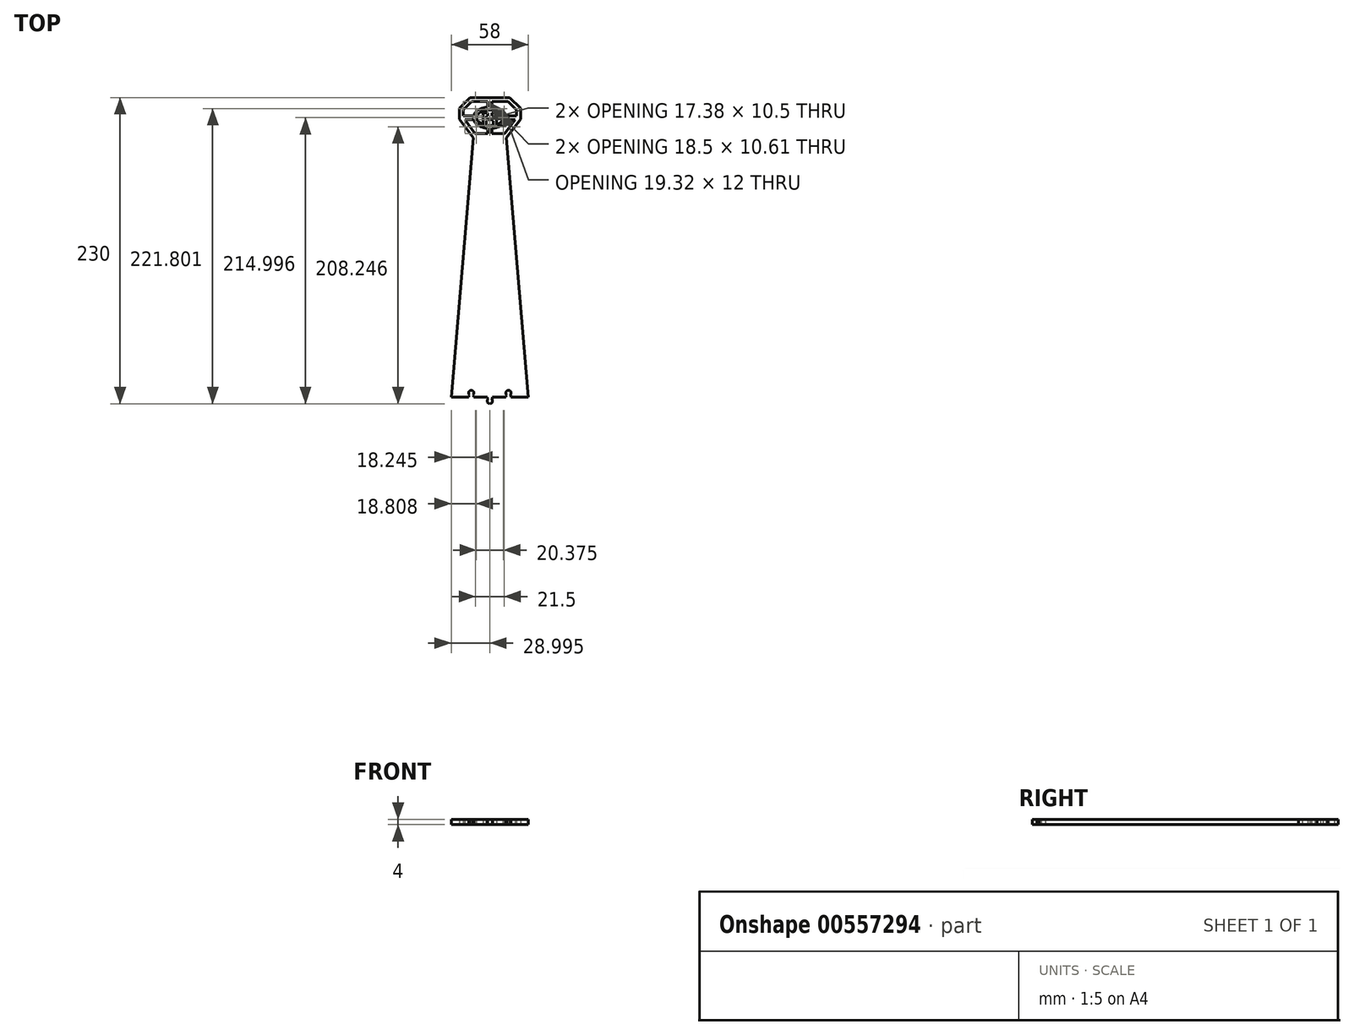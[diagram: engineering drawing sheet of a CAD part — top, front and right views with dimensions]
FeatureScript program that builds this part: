
annotation { "Feature Type Name" : "Feature", "Feature Type Description" : "" }
export const myFeature = defineFeature(function(context is Context, id is Id, definition is map)
    precondition{}
    {
        {
            var Q0;
            Q0=qCreatedBy(makeId("Top.planeOp"),FACE);
            var sketch = newSketch(context, id + "F0", { "sketchPlane" : qUnion([Q0])});
            skLineSegment(sketch, "E0.bottom", {"start": v(14.64, 150.88) * mm, "end": v(-15.36, 150.88) * mm});
            skLineSegment(sketch, "E0.top", {"start": v(12.14, 120.88) * mm, "end": v(-12.86, 120.88) * mm});
            skPoint(sketch, "E0.middle", {"position": v(-0.36, 135.88) * mm});
            skPoint(sketch, "E1", {"position": v(-0.36, 120.88) * mm});
            skPoint(sketch, "E2", {"position": v(-12.86, 120.88) * mm});
            skPoint(sketch, "E3", {"position": v(12.14, 120.88) * mm});
            skLineSegment(sketch, "E4", {"start": v(-15.36, 150.88) * mm, "end": v(-23.36, 142.88) * mm});
            skLineSegment(sketch, "E5", {"start": v(14.64, 150.88) * mm, "end": v(22.64, 142.88) * mm});
            skLineSegment(sketch, "E6", {"start": v(22.64, 142.88) * mm, "end": v(22.64, 134.88) * mm});
            skLineSegment(sketch, "E7", {"start": v(-23.36, 142.88) * mm, "end": v(-23.36, 134.88) * mm});
            skLineSegment(sketch, "E8", {"start": v(-23.36, 134.88) * mm, "end": v(-12.86, 120.88) * mm});
            skLineSegment(sketch, "E9", {"start": v(12.14, 120.88) * mm, "end": v(22.64, 134.88) * mm});
            skPoint(sketch, "E10.orphan", {"position": v(-15.36, 120.88) * mm});
            skEllipticalArc(sketch, "E11", {});
            skEllipticalArc(sketch, "E12", {});
            skLineSegment(sketch, "E13", {"start": v(13.28, 147.99) * mm, "end": v(1.14, 147.99) * mm});
            skLineSegment(sketch, "E14", {"start": v(10.64, 123.88) * mm, "end": v(1.14, 123.88) * mm});
            skLineSegment(sketch, "E15", {"start": v(19.64, 141.63) * mm, "end": v(19.64, 137.38) * mm});
            skLineSegment(sketch, "E16", {"start": v(-11.36, 123.88) * mm, "end": v(-19.24, 134.38) * mm});
            skLineSegment(sketch, "E17", {"start": v(-20.36, 141.63) * mm, "end": v(-20.36, 137.38) * mm});
            skLineSegment(sketch, "E18", {"start": v(-14.01, 147.99) * mm, "end": v(-20.36, 141.63) * mm});
            skLineSegment(sketch, "E19.trimOffspring", {"start": v(19.64, 141.63) * mm, "end": v(13.28, 147.99) * mm});
            skLineSegment(sketch, "E20.trimOffspring", {"start": v(10.64, 123.88) * mm, "end": v(18.51, 134.38) * mm});
            skPoint(sketch, "E21", {"position": v(-0.36, 147.99) * mm});
            skPoint(sketch, "E22", {"position": v(-0.36, 123.88) * mm});
            skPoint(sketch, "E23", {"position": v(-12.86, 135.88) * mm});
            skPoint(sketch, "E24", {"position": v(12.14, 135.88) * mm});
            skLineSegment(sketch, "E25", {"start": v(1.14, 147.99) * mm, "end": v(1.14, 143.82) * mm});
            skLineSegment(sketch, "E26.trimOffspring", {"start": v(1.14, 127.93) * mm, "end": v(1.14, 123.88) * mm});
            skLineSegment(sketch, "E27", {"start": v(-1.86, 147.99) * mm, "end": v(-1.86, 143.82) * mm});
            skLineSegment(sketch, "E28.trimOffspring", {"start": v(-1.86, 127.93) * mm, "end": v(-1.86, 123.88) * mm});
            skLineSegment(sketch, "E29", {"start": v(-20.36, 137.38) * mm, "end": v(-12.64, 137.38) * mm});
            skLineSegment(sketch, "E30", {"start": v(-19.24, 134.38) * mm, "end": v(-12.64, 134.38) * mm});
            skLineSegment(sketch, "E31.trimOffspring", {"start": v(11.91, 134.38) * mm, "end": v(18.51, 134.38) * mm});
            skLineSegment(sketch, "E32.trimOffspring", {"start": v(11.91, 137.38) * mm, "end": v(19.64, 137.38) * mm});
            skLineSegment(sketch, "E33.trimOffspring", {"start": v(-2.86, 137.38) * mm, "end": v(-1.86, 137.38) * mm});
            skPoint(sketch, "E34", {"position": v(-0.36, 137.38) * mm});
            skLineSegment(sketch, "E35", {"start": v(-5.36, 137.38) * mm, "end": v(-5.36, 130.68) * mm});
            skLineSegment(sketch, "E36", {"start": v(4.64, 137.38) * mm, "end": v(4.64, 130.68) * mm});
            skPoint(sketch, "E37.orphan", {"position": v(-10.05, 137.38) * mm});
            skPoint(sketch, "E38.orphan", {"position": v(9.32, 137.38) * mm});
            skLineSegment(sketch, "E39.trimOffspring", {"start": v(1.14, 137.38) * mm, "end": v(2.14, 137.38) * mm});
            skLineSegment(sketch, "E40.trimOffspring", {"start": v(-1.86, 135.38) * mm, "end": v(-1.86, 133.38) * mm});
            skLineSegment(sketch, "E41.trimOffspring", {"start": v(1.14, 135.38) * mm, "end": v(1.14, 133.38) * mm});
            skLineSegment(sketch, "E42", {"start": v(2.14, 135.38) * mm, "end": v(1.14, 135.38) * mm});
            skLineSegment(sketch, "E43", {"start": v(2.14, 133.38) * mm, "end": v(1.14, 133.38) * mm});
            skPoint(sketch, "E44", {"position": v(-0.36, 133.38) * mm});
            skLineSegment(sketch, "E45", {"start": v(-2.86, 133.38) * mm, "end": v(-2.86, 130.07) * mm});
            skLineSegment(sketch, "E46", {"start": v(2.14, 133.38) * mm, "end": v(2.14, 130.07) * mm});
            skLineSegment(sketch, "E47", {"start": v(4.64, 137.38) * mm, "end": v(4.64, 139.38) * mm});
            skLineSegment(sketch, "E48", {"start": v(-5.36, 137.38) * mm, "end": v(-5.36, 139.38) * mm});
            skLineSegment(sketch, "E49", {"start": v(4.64, 139.38) * mm, "end": v(1.14, 139.38) * mm});
            skLineSegment(sketch, "E50", {"start": v(-1.86, 137.38) * mm, "end": v(-1.86, 139.38) * mm});
            skLineSegment(sketch, "E51", {"start": v(1.14, 137.38) * mm, "end": v(1.14, 139.38) * mm});
            skLineSegment(sketch, "E52", {"start": v(2.14, 135.38) * mm, "end": v(2.14, 137.38) * mm});
            skLineSegment(sketch, "E53", {"start": v(-2.86, 135.38) * mm, "end": v(-2.86, 137.38) * mm});
            skLineSegment(sketch, "E54.trimOffspring", {"start": v(-1.86, 139.38) * mm, "end": v(-5.36, 139.38) * mm});
            skLineSegment(sketch, "E55.trimOffspring", {"start": v(-1.86, 135.38) * mm, "end": v(-2.86, 135.38) * mm});
            skLineSegment(sketch, "E56.trimOffspring", {"start": v(-1.86, 133.38) * mm, "end": v(-2.86, 133.38) * mm});
            skPoint(sketch, "E57.orphan", {"position": v(-5.36, 133.38) * mm});
            skPoint(sketch, "E58.orphan", {"position": v(4.64, 133.38) * mm});
            skEllipticalArc(sketch, "E59.trimOffspring", {});
            skLineSegment(sketch, "E60.trimOffspring", {"start": v(-1.86, 123.88) * mm, "end": v(-11.36, 123.88) * mm});
            skEllipticalArc(sketch, "E61.trimOffspring", {});
            skEllipticalArc(sketch, "E62.trimOffspring", {});
            skEllipticalArc(sketch, "E63.trimOffspring", {});
            skLineSegment(sketch, "E64.trimOffspring", {"start": v(-1.86, 147.99) * mm, "end": v(-14.01, 147.99) * mm});
            skLineSegment(sketch, "E65.bottom", {"start": v(-12.86, 120.88) * mm, "end": v(12.14, 120.88) * mm});
            skPoint(sketch, "E66", {"position": v(-0.36, -74.12) * mm});
            skLineSegment(sketch, "E67", {"start": v(28.64, -74.12) * mm, "end": v(15.64, -74.12) * mm});
            skLineSegment(sketch, "E68", {"start": v(-29.36, -74.12) * mm, "end": v(-12.86, 120.88) * mm});
            skLineSegment(sketch, "E69", {"start": v(28.64, -74.12) * mm, "end": v(12.14, 120.88) * mm});
            skPoint(sketch, "E70", {"position": v(-14.36, -74.12) * mm});
            skPoint(sketch, "E71", {"position": v(13.64, -74.12) * mm});
            skLineSegment(sketch, "E72", {"start": v(-16.36, -74.12) * mm, "end": v(-16.36, -73.12) * mm});
            skLineSegment(sketch, "E73", {"start": v(-12.36, -74.12) * mm, "end": v(-12.36, -73.12) * mm});
            skLineSegment(sketch, "E74", {"start": v(15.64, -74.12) * mm, "end": v(15.64, -73.12) * mm});
            skLineSegment(sketch, "E75", {"start": v(11.64, -74.12) * mm, "end": v(11.64, -73.12) * mm});
            skPoint(sketch, "E76", {"position": v(-14.36, -71.12) * mm});
            skPoint(sketch, "E77", {"position": v(13.64, -71.12) * mm});
            skArc(sketch, "E78", {"start": v(-12.95, -72.54) * mm, "mid": v(-14.36, -69.12) * mm, "end": v(-15.78, -72.54) * mm});
            skArc(sketch, "E79", {"start": v(15.05, -72.54) * mm, "mid": v(13.64, -69.12) * mm, "end": v(12.22, -72.54) * mm});
            skLineSegment(sketch, "E80", {"start": v(11.64, -73.12) * mm, "end": v(12.22, -72.54) * mm});
            skLineSegment(sketch, "E81", {"start": v(15.64, -73.12) * mm, "end": v(15.05, -72.54) * mm});
            skLineSegment(sketch, "E82", {"start": v(-12.36, -73.12) * mm, "end": v(-12.95, -72.54) * mm});
            skLineSegment(sketch, "E83", {"start": v(-16.36, -73.12) * mm, "end": v(-15.78, -72.54) * mm});
            skArc(sketch, "E84", {"start": v(-1.78, -75.71) * mm, "mid": v(-0.36, -79.12) * mm, "end": v(1.05, -75.71) * mm});
            skLineSegment(sketch, "E85", {"start": v(-2.36, -74.12) * mm, "end": v(-2.36, -75.12) * mm});
            skLineSegment(sketch, "E86", {"start": v(1.64, -74.12) * mm, "end": v(1.64, -75.12) * mm});
            skLineSegment(sketch, "E87", {"start": v(-2.36, -75.12) * mm, "end": v(-1.78, -75.71) * mm});
            skLineSegment(sketch, "E88", {"start": v(1.64, -75.12) * mm, "end": v(1.05, -75.71) * mm});
            skPoint(sketch, "E89.orphan", {"position": v(-2.36, -79.12) * mm});
            skPoint(sketch, "E90.trimOffspring.end.orphan", {"position": v(-0.36, -79.12) * mm});
            skLineSegment(sketch, "E91.trimOffspring", {"start": v(-2.36, -74.12) * mm, "end": v(-12.36, -74.12) * mm});
            skLineSegment(sketch, "E92.trimOffspring", {"start": v(-16.36, -74.12) * mm, "end": v(-29.36, -74.12) * mm});
            skPoint(sketch, "E93.orphan", {"position": v(-12.36, -71.12) * mm});
            skPoint(sketch, "E94.trimOffspring.end.orphan", {"position": v(-16.36, -71.12) * mm});
            skLineSegment(sketch, "E95.trimOffspring", {"start": v(11.64, -74.12) * mm, "end": v(1.64, -74.12) * mm});
            skPoint(sketch, "E96.orphan", {"position": v(11.64, -71.12) * mm});
            skPoint(sketch, "E97.start.orphan", {"position": v(15.64, -71.12) * mm});
            const initialGuessF0  = {"E11": [-0.0003648042464688972, 0.13587578032428296, 1, 0, 0.0125, 0.008, 4.832678862779479, 6.094568921004184], "E12": [-0.0003648042464688972, 0.13587578032428296, 1, 0, 0.01, 0.006, 5.235987755982989, 4.188790204786391], "E59.trimOffspring": [-0.0003648042464688972, 0.13587578032428296, 1, 0, 0.01, 0.006, 4.459708725242612, 4.9650692355267685], "E61.trimOffspring": [-0.0003648042464688972, 0.13587578032428296, 1, 0, 0.0125, 0.008, 1.6910862091896828, 2.952976267414389], "E62.trimOffspring": [-0.0003648042464688972, 0.13587578032428296, 1, 0, 0.0125, 0.008, 0.18861638617540466, 1.4505064444001077], "E63.trimOffspring": [-0.0003648042464688972, 0.13587578032428296, 1, 0, 0.0125, 0.008, 3.330209039765196, 4.592099097989903]};
            skSetInitialGuess(sketch, initialGuessF0);
            skSolve(sketch);
        }
        {
            var Q0;
            Q0 = qSketchRegion(id + "F0", true);
            extrude(context, id + "F1", {"entities" : qUnion([Q0]), "depth" : 4 * mm, "offsetDistance" : 25 * mm});
        }
    });
